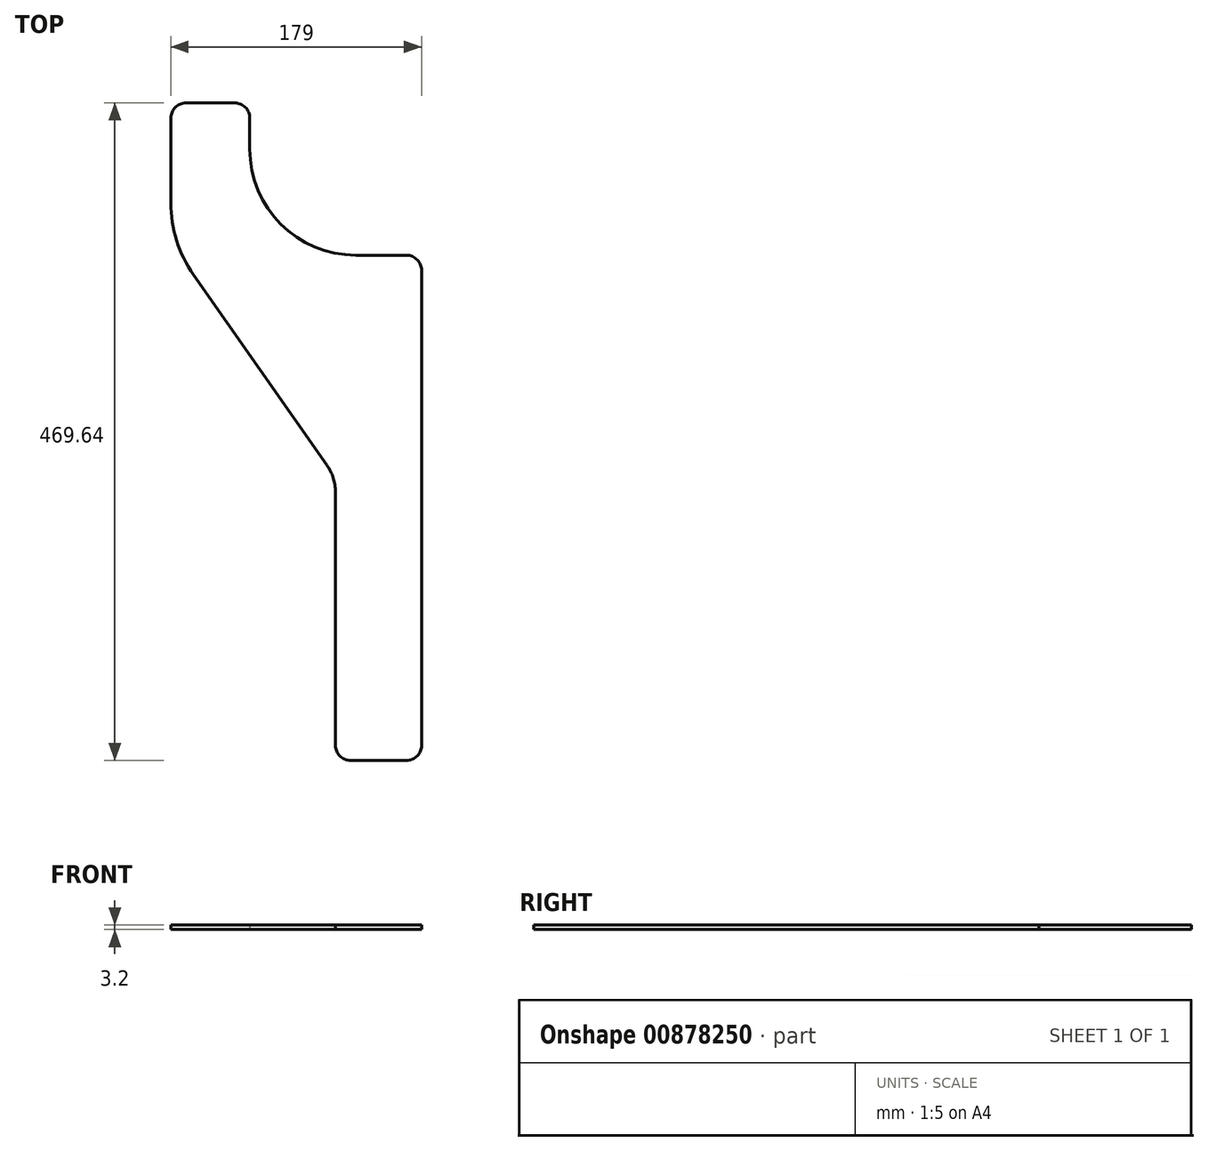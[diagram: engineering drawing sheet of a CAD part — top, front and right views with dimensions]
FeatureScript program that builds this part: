
annotation { "Feature Type Name" : "Feature", "Feature Type Description" : "" }
export const myFeature = defineFeature(function(context is Context, id is Id, definition is map)
    precondition{}
    {
        {
            var Q0;
            Q0=qCreatedBy(makeId("Top.planeOp"),FACE);
            var sketch = newSketch(context, id + "F0", { "sketchPlane" : qUnion([Q0])});
            skArc(sketch, "E0", {"start": v(0, 10.8) * mm, "mid": v(3.16, 3.16) * mm, "end": v(10.8, 0) * mm});
            skLineSegment(sketch, "E1", {"start": v(10.8, 0) * mm, "end": v(50.7, 0) * mm});
            skArc(sketch, "E2", {"start": v(50.7, 0) * mm, "mid": v(58.34, 3.16) * mm, "end": v(61.5, 10.8) * mm});
            skLineSegment(sketch, "E3", {"start": v(61.5, 10.8) * mm, "end": v(61.5, 350.02) * mm});
            skArc(sketch, "E4", {"start": v(61.5, 350.02) * mm, "mid": v(58.34, 357.66) * mm, "end": v(50.7, 360.82) * mm});
            skLineSegment(sketch, "E5", {"start": v(50.7, 360.82) * mm, "end": v(14.7, 360.82) * mm});
            skArc(sketch, "E6", {"start": v(-61.2, 436.72) * mm, "mid": v(-38.97, 383.05) * mm, "end": v(14.7, 360.82) * mm});
            skLineSegment(sketch, "E7", {"start": v(-61.2, 436.72) * mm, "end": v(-61.2, 458.84) * mm});
            skArc(sketch, "E8", {"start": v(-61.2, 458.84) * mm, "mid": v(-64.36, 466.48) * mm, "end": v(-72, 469.64) * mm});
            skLineSegment(sketch, "E9", {"start": v(-72, 469.64) * mm, "end": v(-106.7, 469.64) * mm});
            skArc(sketch, "E10", {"start": v(-106.7, 469.64) * mm, "mid": v(-114.34, 466.48) * mm, "end": v(-117.5, 458.84) * mm});
            skLineSegment(sketch, "E11", {"start": v(-117.5, 458.84) * mm, "end": v(-117.5, 398.25) * mm});
            skArc(sketch, "E12", {"start": v(-117.5, 398.25) * mm, "mid": v(-113.36, 371.34) * mm, "end": v(-101.31, 346.92) * mm});
            skLineSegment(sketch, "E13", {"start": v(-101.31, 346.92) * mm, "end": v(-6, 210.8) * mm});
            skArc(sketch, "E14", {"start": v(0, 191.76) * mm, "mid": v(-1.54, 201.74) * mm, "end": v(-6, 210.8) * mm});
            skLineSegment(sketch, "E15", {"start": v(0, 10.8) * mm, "end": v(0, 191.76) * mm});
            skLineSegment(sketch, "E16", {"start": v(-33.2, 191.76) * mm, "end": v(0, 191.76) * mm, "construction": true});
            skLineSegment(sketch, "E17", {"start": v(-33.2, 191.76) * mm, "end": v(-6, 210.8) * mm, "construction": true});
            skSolve(sketch);
        }
        {
            var Q0;
            Q0=makeQuery(id+"F0.imprint","IMPRINT",FACE,{"disambiguationData":[TD([[makeQuery(id+"F0.imprint","IMPRINT",EDGE,{"derivedFrom":sQuery(id+"F0.wireOp",EDGE,"E0")}),1.0]])]});
            extrude(context, id + "F1", {"entities" : qUnion([Q0]), "depth" : 3.2 * mm, "offsetDistance" : 25 * mm});
        }
    });
